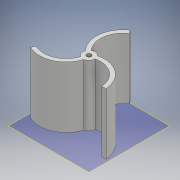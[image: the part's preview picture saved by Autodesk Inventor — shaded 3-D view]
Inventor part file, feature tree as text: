
AUTODESK INVENTOR PART (.ipt)
format: ipt  version: 2017 (Build 210142000, 142)  size: 187,392 bytes
history: native  units: mm
features: other x2, extrude x2, sketch x2, plane x1
ambient origin geometry x8: Origin, YZ Plane, XZ Plane, XY Plane, X Axis, Y Axis, Z Axis, Center Point
bodies: Solid1 (feature_tree)
feature tree (7):
  other  "Impeller"
  plane  "Work Plane1"
  extrude  "Extrusion1"  Depth=15.0mm TaperAngle=0.0deg
  extrude  "Extrusion2"  [1 undecoded]
  sketch  "Sketch4"  dims[d3=15.0mm d4=0.0mm]
  sketch  "Sketch1"  dims[d0=0.0mm d1=15.0mm d2=0.0mm]
  other  "MeshFeature1"
note: 1 required parameter value undecoded (feature->parameter linkage not recoverable at this tier; creation-order binding heuristic only, values carry confidence <= 0.55)
